# Revit family: XWD
name_source: partatom
category: Mechanical Equipment
units: mm (PartAtom-declared; Revit-internal decimal feet)

## family parameters
Always vertical = Yes
Cut with Voids When Loaded = No
Part Type = Normal
Room Calculation Point = No
Round Connector Dimension = Use Diameter
Shared = No
Work Plane-Based = No

## types (8) — shared parameters
(E-C)/2 = 0' - 1"
-D = -0' - 2"
0 = 0' - 0"
1" = 0' - 1"
1.5 = 0' - 1 1/2"
1/2 = 0' - 0 1/2"
2" = 0' - 2"
2' = 2' - 0"
3" = 0' - 3"
4" = 0' - 4"
9" = 0' - 9"
EMINUSC = 0' - 2"
Manufacturer = Loren Cook Company
Model = AWD
ONE EIGTH = 0' - 0 1/8"
Type Comments = Wall Exhaust Fan Cast Aluminum Propeller Direct Drive
URL = www.lorencook.com

## per-type parameters (varying)
| type | (A/2)-1" | (A/2)-C-.5" | (D-.25")/2 | (SIZE/2)-.25" | -((A/2)-C-.5") | -((SIZE/2)-.25") | -B | -B+1" | -C/2 | A | A/2 | A/3.5 | A/7 | B | B/2 | C | C+F | C/2 | D | D/2 | F | SIZE | SIZE/2 |
| 12_XWD | 0' - 7 27/32" | 0' - 5 27/32" | 0' - 6 1/8" | 0' - 5 3/4" | -0' - 5 27/32" | -0' - 5 3/4" | -0' - 7 1/2" | -0' - 6 1/2" | -0' - 0 7/8" | 1' - 4 3/16" | 0' - 8 3/32" | 0' - 4 5/8" | 0' - 2 5/16" | 0' - 7 1/2" | 0' - 3 3/4" | 0' - 1 3/4" | 0' - 2 13/16" | 0' - 0 7/8" | 1' - 0 1/2" | 0' - 6 1/4" | 0' - 1 1/16" | 1' - 0" | 0' - 6" |
| 16_XWD | 0' - 9 27/32" | 0' - 7 3/32" | 0' - 8 1/8" | 0' - 7 3/4" | -0' - 7 3/32" | -0' - 7 3/4" | -0' - 8 1/2" | -0' - 7 1/2" | -0' - 1 1/4" | 1' - 8 3/16" | 0' - 10 3/32" | 0' - 5 25/32" | 0' - 2 7/8" | 0' - 8 1/2" | 0' - 4 1/4" | 0' - 2 1/2" | 0' - 3 3/4" | 0' - 1 1/4" | 1' - 4 1/2" | 0' - 8 1/4" | 0' - 1 1/4" | 1' - 4" | 0' - 8" |
| 20_XWD | 0' - 11 27/32" | 0' - 8 27/32" | 0' - 10 3/16" | 0' - 9 3/4" | -0' - 8 27/32" | -0' - 9 3/4" | -0' - 9 3/4" | -0' - 8 3/4" | -0' - 1 3/8" | 2' - 0 3/16" | 1' - 0 3/32" | 0' - 6 29/32" | 0' - 3 15/32" | 0' - 9 3/4" | 0' - 4 7/8" | 0' - 2 3/4" | 0' - 4 1/8" | 0' - 1 3/8" | 1' - 8 5/8" | 0' - 10 5/16" | 0' - 1 3/8" | 1' - 8" | 0' - 10" |
| 24_XWD | 1' - 2 27/32" | 0' - 11 27/32" | 1' - 0 1/4" | 0' - 11 3/4" | -0' - 11 27/32" | -0' - 11 3/4" | -0' - 9 3/4" | -0' - 8 3/4" | -0' - 1 3/8" | 2' - 6 3/16" | 1' - 3 3/32" | 0' - 8 5/8" | 0' - 4 5/16" | 0' - 9 3/4" | 0' - 4 7/8" | 0' - 2 3/4" | 0' - 4 1/16" | 0' - 1 3/8" | 2' - 0 3/4" | 1' - 0 3/8" | 0' - 1 5/16" | 2' - 0" | 1' - 0" |
| 14_XWD | 0' - 9 27/32" | 0' - 7 3/32" | 0' - 7 1/8" | 0' - 6 3/4" | -0' - 7 3/32" | -0' - 6 3/4" | -0' - 8 1/2" | -0' - 7 1/2" | -0' - 1 1/4" | 1' - 8 3/16" | 0' - 10 3/32" | 0' - 5 25/32" | 0' - 2 7/8" | 0' - 8 1/2" | 0' - 4 1/4" | 0' - 2 1/2" | 0' - 3 7/8" | 0' - 1 1/4" | 1' - 2 1/2" | 0' - 7 1/4" | 0' - 1 3/8" | 1' - 2" | 0' - 7" |
| 18_XWD | 0' - 11 27/32" | 0' - 8 27/32" | 0' - 9 1/8" | 0' - 8 3/4" | -0' - 8 27/32" | -0' - 8 3/4" | -0' - 9 3/4" | -0' - 8 3/4" | -0' - 1 3/8" | 2' - 0 3/16" | 1' - 0 3/32" | 0' - 6 29/32" | 0' - 3 15/32" | 0' - 9 3/4" | 0' - 4 7/8" | 0' - 2 3/4" | 0' - 4" | 0' - 1 3/8" | 1' - 6 1/2" | 0' - 9 1/4" | 0' - 1 1/4" | 1' - 6" | 0' - 9" |
| 10_XWD | 0' - 7 27/32" | 0' - 6 3/32" | 0' - 5 1/8" | 0' - 4 3/4" | -0' - 6 3/32" | -0' - 4 3/4" | -0' - 5 1/2" | -0' - 4 1/2" | -0' - 0 3/4" | 1' - 4 3/16" | 0' - 8 3/32" | 0' - 4 5/8" | 0' - 2 5/16" | 0' - 5 1/2" | 0' - 2 3/4" | 0' - 1 1/2" | 0' - 2 5/8" | 0' - 0 3/4" | 0' - 10 1/2" | 0' - 5 1/4" | 0' - 1 1/8" | 0' - 10" | 0' - 5" |
| 8_XWD | 0' - 5 27/32" | 0' - 4 19/32" | 0' - 4 1/8" | 0' - 3 3/4" | -0' - 4 19/32" | -0' - 3 3/4" | -0' - 4 3/4" | -0' - 3 3/4" | -0' - 0 1/2" | 1' - 0 3/16" | 0' - 6 3/32" | 0' - 3 15/32" | 0' - 1 3/4" | 0' - 4 3/4" | 0' - 2 3/8" | 0' - 1" | 0' - 1 1/2" | 0' - 0 1/2" | 0' - 8 1/2" | 0' - 4 1/4" | 0' - 0 1/2" | 0' - 8" | 0' - 4" |

## geometry (parser evidence)
native form markers: Sweep x2
no freeform markers — native parametric forms only
